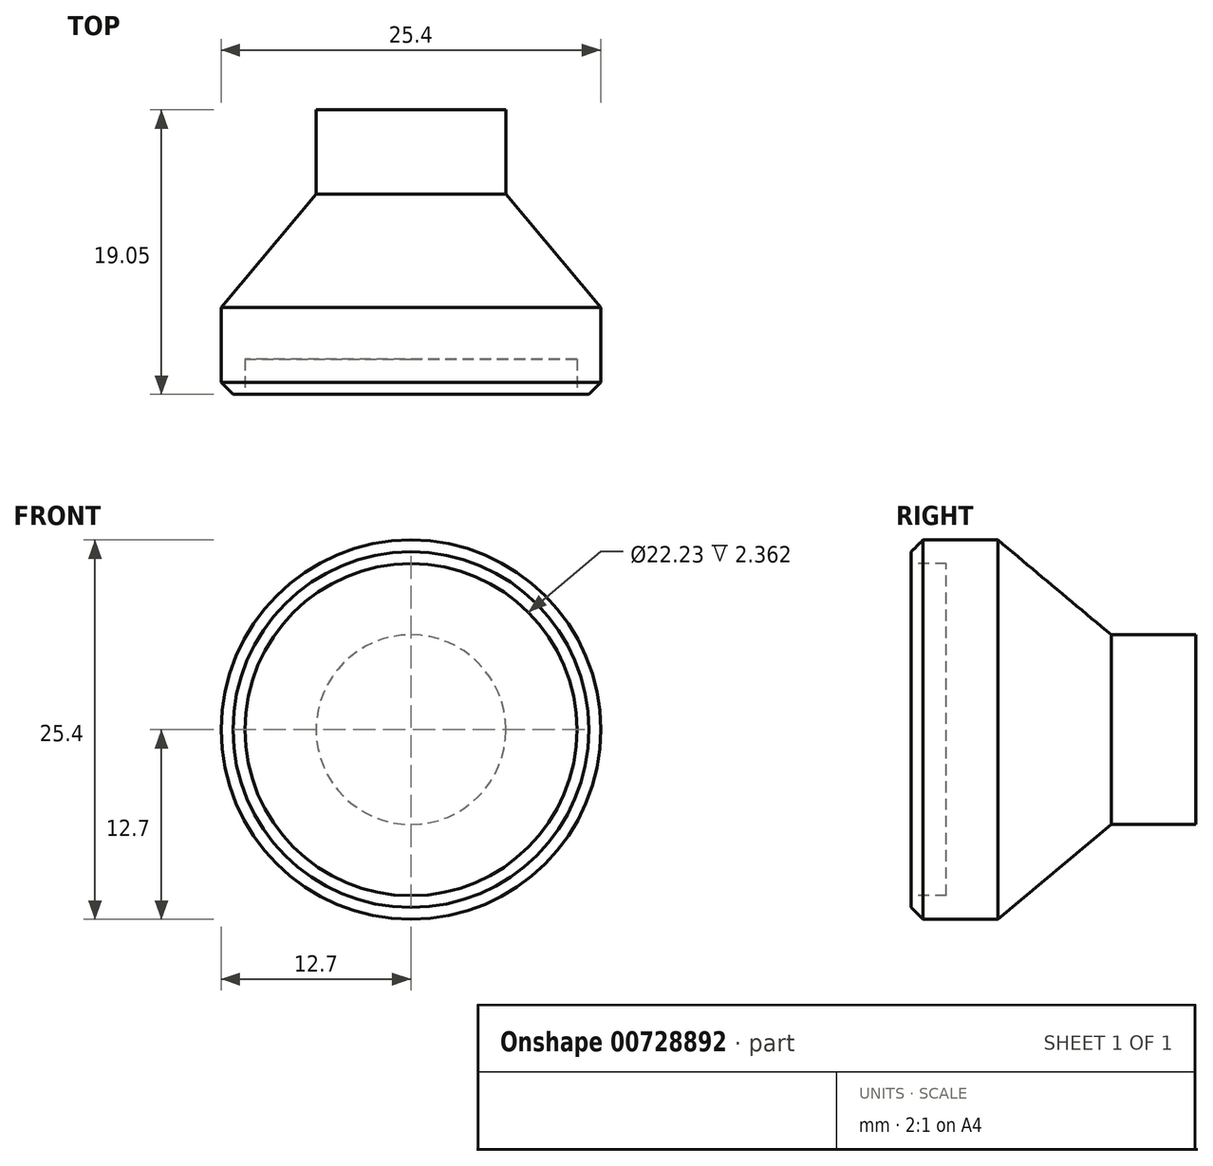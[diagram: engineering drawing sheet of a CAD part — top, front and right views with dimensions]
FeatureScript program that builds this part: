
annotation { "Feature Type Name" : "Feature", "Feature Type Description" : "" }
export const myFeature = defineFeature(function(context is Context, id is Id, definition is map)
    precondition{}
    {
        {
            var Q0;
            Q0=qCreatedBy(makeId("Right.planeOp"),FACE);
            var sketch = newSketch(context, id + "F0", { "sketchPlane" : qUnion([Q0])});
            skLineSegment(sketch, "E0", {"start": v(0, 0) * mm, "end": v(0, 12.7) * mm});
            skLineSegment(sketch, "E1", {"start": v(0, 12.7) * mm, "end": v(5.8, 12.7) * mm});
            skLineSegment(sketch, "E2", {"start": v(5.8, 12.7) * mm, "end": v(13.4, 6.35) * mm});
            skLineSegment(sketch, "E3", {"start": v(13.4, 6.35) * mm, "end": v(19.05, 6.35) * mm});
            skLineSegment(sketch, "E4", {"start": v(19.05, 6.35) * mm, "end": v(19.05, 0) * mm});
            skLineSegment(sketch, "E5", {"start": v(19.05, 0) * mm, "end": v(0, 0) * mm});
            skSolve(sketch);
        }
        {
            var Q0;
            Q0 = qSketchRegion(id + "F0", true);
            var Q1;
            Q1=sQuery(id+"F0.wireOp",EDGE,"E5");
            revolve(context, id + "F1", {"surfaceOperationType" : NewSurfaceOperationType.NEW, "entities" : qUnion([Q0]), "axis" : qUnion([Q1]), "revolveType" : RevolveType.FULL});
        }
        {
            var Q0;
            Q0=makeQuery(id+"F1.opRevolve","SWEPT_EDGE",EDGE,{"disambiguationData":[OSD([sQuery(id+"F0.wireOp",EDGE,"E0"),sQuery(id+"F0.wireOp",EDGE,"E1")])]});
            chamfer(context, id + "F2", {"entities" : qUnion([Q0]), "width" : 0.8 * mm, "tangentPropagation" : true});
        }
        {
            var Q0;
            Q0=makeQuery(id+"F1.opRevolve","SWEPT_FACE",FACE,{"disambiguationData":[OSD([sQuery(id+"F0.wireOp",EDGE,"E0")])]});
            var sketch = newSketch(context, id + "F3", { "sketchPlane" : qUnion([Q0])});
            skCircle(sketch, "E6", {"center": v(0, 0) * mm, "radius": 11.11 * mm});
            skSolve(sketch);
        }
        {
            var Q0;
            Q0 = qSketchRegion(id + "F3", true);
            extrude(context, id + "F4", {"entities" : qUnion([Q0]), "operationType" : NewBodyOperationType.REMOVE, "oppositeDirection" : true, "depth" : 2.36 * mm, "offsetDistance" : 25.4 * mm});
        }
    });
